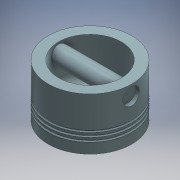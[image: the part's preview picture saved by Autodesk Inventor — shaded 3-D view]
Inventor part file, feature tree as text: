
AUTODESK INVENTOR PART (.ipt)
format: ipt  version: 2016 (Build 200138000, 138)  size: 204,288 bytes
history: native  units: mm
features: extrude x4, sketch x4, plane x2, shell x1, fillet x1, mirror x1, pattern_linear x1, projected_geometry x1
ambient origin geometry x8: Origin, YZ Plane, XZ Plane, XY Plane, X Axis, Y Axis, Z Axis, Center Point
bodies: Solid1 (feature_tree)
feature tree (15):
  extrude  "Extrusion1"  Depth=5.0mm TaperAngle=0.0deg
  shell  "Shell1"  Thickness=5.0mm
  fillet  "Fillet1"  Radius=5.0mm
  extrude  "Extrusion2"  Depth=5.0mm
  plane  "Work Plane1"
  extrude  "Extrusion3"  Depth=18.0mm
  mirror  "Mirror1"
  plane  "Work Plane2"
  extrude  "Extrusion4"  Depth=2.0mm TaperAngle=0.0deg
  pattern_linear  "Rectangular Pattern1"  Spacing1=5.0mm  [1 undecoded]
  sketch  "Sketch1"  dims[d0=40.0mm d1=25.0mm d2=0.0mm d3=5.0mm d4=5.0mm]
  sketch  "Sketch2"  dims[d5=8.0mm d6=5.0mm]
  sketch  "Sketch3"  dims[d7=25.0mm d8=0.0mm d9=18.0mm]
  sketch  "Sketch4"  dims[d10=0.0mm d11=25.0mm d12=0.0mm d13=5.0mm d14=1.0mm d15=1.0mm d16=0.0mm d17=30.0mm d19=2.0mm]
  projected_geometry  "Projected Loop1"
note: 1 required parameter value undecoded (feature->parameter linkage not recoverable at this tier; creation-order binding heuristic only, values carry confidence <= 0.55)
